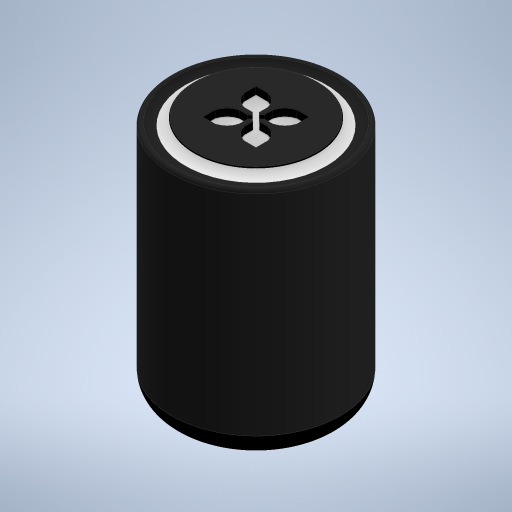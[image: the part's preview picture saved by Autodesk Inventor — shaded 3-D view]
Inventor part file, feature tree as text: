
AUTODESK INVENTOR PART (.ipt)
format: ipt  version: 2024 (Build 280153000, 153)  size: 346,112 bytes
history: native  units: in
note: dims shown in document units (in); Inventor stores cm internally (conversion verified against a paired STEP export)
features: sketch x2, revolve x1, extrude x1, fillet x1
ambient origin geometry x8: Origin, YZ Plane, XZ Plane, XY Plane, X Axis, Y Axis, Z Axis, Center Point
bodies: Solid1 (feature_tree)
feature tree (5):
  revolve  "Revolution1"  [1 undecoded]
  extrude  "Extrusion1"  Depth=0.3937in
  fillet  "Fillet1"  Radius=0.3937in
  sketch  "Sketch1"  dims[d0=1.378in d1=3.937in]
  sketch  "Sketch2"  dims[d2=90.0deg d3=0.3937in d4=0.3937in d5=0.3937in d6=0.0394in d7=0.0394in d8=0.2756in d10=0.2756in d11=1.5748in d13=360.0deg d15=0.1181in d16=0.0in d17=0.0394in d18=0.0394in d19=0.0394in d20=-0.0394in d21=0.0492in]
note: 1 required parameter value undecoded (feature->parameter linkage not recoverable at this tier; creation-order binding heuristic only, values carry confidence <= 0.55)
